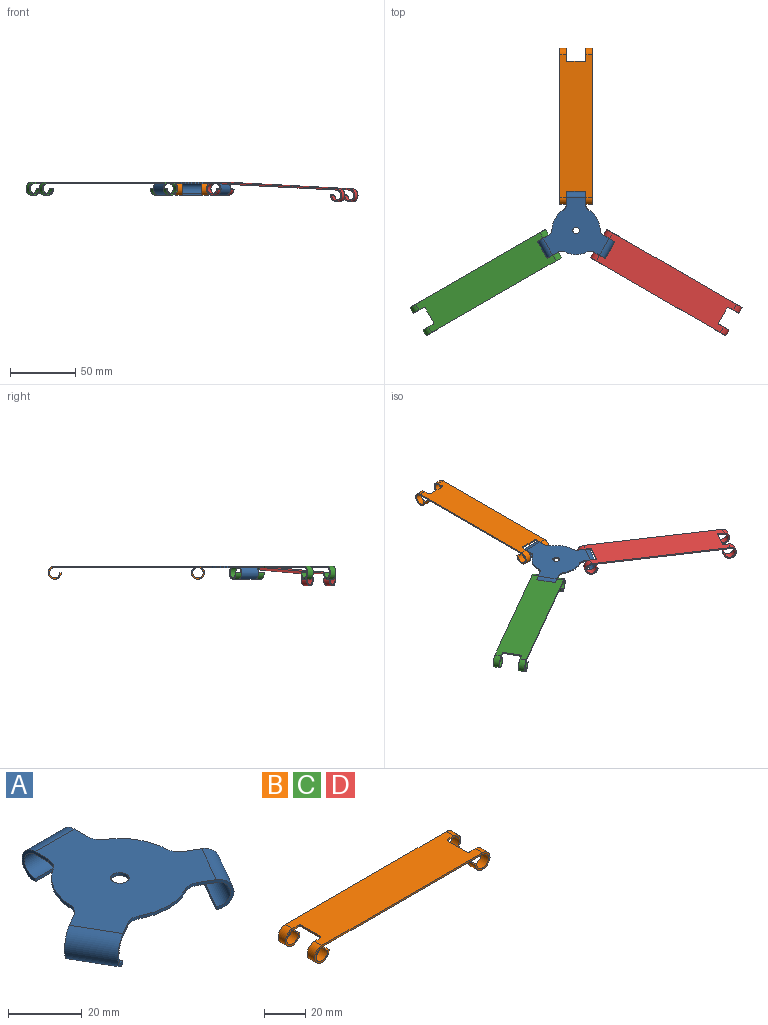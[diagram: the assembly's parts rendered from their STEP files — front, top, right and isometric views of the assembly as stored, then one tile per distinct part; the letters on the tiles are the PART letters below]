
ASSEMBLY  parts=4 mates=3
PART A: 27 faces, bbox 59.5x51.5x10 mm
  f0: cylinder r=18.5mm len=14.98mm, axis (0,0,1), area 18mm2, adj f12,f16,f20,f25
  f1: plane 10x8.75mm, normal (0.5,0.87,0), area 19.2mm2, adj f10,f12,f15,f16,f19,f25
  f2: plane 10x8.75mm, normal (-0.5,-0.87,0), area 19.2mm2, adj f10,f12,f15,f16,f19,f24
  f3: cylinder r=18.5mm len=17.29mm, axis (0,0,1), area 18mm2, adj f12,f16,f23,f24
  f4: plane 10x8.75mm, normal (0.5,-0.87,0), area 19.2mm2, adj f9,f12,f14,f16,f18,f23
  f5: plane 10x8.75mm, normal (-0.5,0.87,0), area 19.2mm2, adj f9,f12,f14,f16,f18,f22
  f6: cylinder r=18.5mm len=14.98mm, axis (0,0,1), area 18mm2, adj f12,f16,f21,f22
  f7: plane 10.1x10mm, normal (-1,0,0), area 19.2mm2, adj f11,f12,f13,f16,f17,f21
  f8: plane 10.1x10mm, normal (1,0,0), area 19.2mm2, adj f11,f12,f13,f16,f17,f20
  f9: plane 12.99x7.5mm, normal (0.87,0.5,0), area 15mm2, adj f4,f5,f14,f18
  f10: plane 12.99x7.5mm, normal (-0.87,0.5,0), area 15mm2, adj f1,f2,f15,f19
  f11: plane 15x1mm, normal (0,-1,0), area 15mm2, adj f7,f8,f13,f17
  f12: plane 50.8x44mm, normal (0,0,1), area 1379.7mm2, adj f0,f1,f2,f3,f4,f5,f6,f7
  f13: cylinder r=5mm len=15mm, axis (1,0,0), area 235.6mm2, adj f7,f8,f11,f12
  f14: cylinder r=5mm len=15.49mm, axis (-0.5,0.87,0), area 235.6mm2, adj f4,f5,f9,f12
  f15: cylinder r=5mm len=15.49mm, axis (-0.5,-0.87,0), area 235.6mm2, adj f1,f2,f10,f12
  f16: plane 50.8x44mm, normal (0,0,-1), area 1379.7mm2, adj f0,f1,f2,f3,f4,f5,f6,f7
  f17: cylinder r=4mm len=15mm, axis (1,0,0), area 188.5mm2, adj f7,f8,f11,f16
  f18: cylinder r=4mm len=14.99mm, axis (-0.5,0.87,0), area 188.5mm2, adj f4,f5,f9,f16
  f19: cylinder r=4mm len=14.99mm, axis (-0.5,-0.87,0), area 188.5mm2, adj f1,f2,f10,f16
  f20: cylinder r=5mm len=4.23mm, axis (0,0,1), area 5mm2, adj f0,f8,f12,f16
  f21: cylinder r=5mm len=4.23mm, axis (0,0,1), area 5mm2, adj f6,f7,f12,f16
  f22: cylinder r=5mm len=4.14mm, axis (0,0,1), area 5mm2, adj f5,f6,f12,f16
  f23: cylinder r=5mm len=4.84mm, axis (0,0,1), area 5mm2, adj f3,f4,f12,f16
  f24: cylinder r=5mm len=4.84mm, axis (0,0,1), area 5mm2, adj f2,f3,f12,f16
  f25: cylinder r=5mm len=4.14mm, axis (0,0,1), area 5mm2, adj f0,f1,f12,f16
  f26: cylinder r=2.5mm len=5mm, axis (0,0,1), area 15.7mm2, adj f12,f16
PART B: 26 faces, bbox 120x25x10 mm
  f0: cylinder r=4mm len=8mm, axis (0,1,0), area 94.2mm2, adj f1,f7,f15,f17
  f1: plane 110x25mm, normal (0,0,-1), area 2600.9mm2, adj f0,f2,f8,f9,f14,f15,f16,f17
  f2: cylinder r=4mm len=8mm, axis (0,1,0), area 94.2mm2, adj f1,f3,f14,f20
  f3: plane 5x1mm, normal (0,0,1), area 5mm2, adj f2,f4,f14,f20
  f4: cylinder r=5mm len=10mm, axis (0,1,0), area 117.8mm2, adj f3,f5,f14,f20
  f5: plane 110x25mm, normal (0,0,1), area 2600.9mm2, adj f4,f6,f11,f12,f14,f15,f16,f17
  f6: cylinder r=5mm len=10mm, axis (0,1,0), area 117.8mm2, adj f5,f7,f15,f17
  f7: plane 5x1mm, normal (0,0,1), area 5mm2, adj f0,f6,f15,f17
  f8: cylinder r=4mm len=8mm, axis (0,1,0), area 94.2mm2, adj f1,f13,f14,f18
  f9: cylinder r=4mm len=8mm, axis (0,1,0), area 94.2mm2, adj f1,f10,f15,f19
  f10: plane 5x1mm, normal (0,0,1), area 5mm2, adj f9,f11,f15,f19
  f11: cylinder r=5mm len=10mm, axis (0,1,0), area 117.8mm2, adj f5,f10,f15,f19
  f12: cylinder r=5mm len=10mm, axis (0,1,0), area 117.8mm2, adj f5,f13,f14,f18
  f13: plane 5x1mm, normal (0,0,1), area 5mm2, adj f8,f12,f14,f18
  f14: plane 120x10mm, normal (0,-1,0), area 152.4mm2, adj f1,f2,f3,f4,f5,f8,f12,f13
  f15: plane 120x10mm, normal (0,1,0), area 152.4mm2, adj f0,f1,f5,f6,f7,f9,f10,f11
  f16: plane 13x1mm, normal (-1,0,0), area 13mm2, adj f1,f5,f24,f25
  f17: plane 10x10mm, normal (0,-1,0), area 25.2mm2, adj f0,f1,f5,f6,f7,f25
  f18: plane 10x10mm, normal (0,1,0), area 25.2mm2, adj f1,f5,f8,f12,f13,f24
  f19: plane 10x10mm, normal (0,-1,0), area 25.2mm2, adj f1,f5,f9,f10,f11,f22
  f20: plane 10x10mm, normal (0,1,0), area 25.2mm2, adj f1,f2,f3,f4,f5,f23
  f21: plane 13x1mm, normal (1,0,0), area 13mm2, adj f1,f5,f22,f23
  f22: cylinder r=1mm len=1mm, axis (0,0,-1), area 1.6mm2, adj f1,f5,f19,f21
  f23: cylinder r=1mm len=1mm, axis (0,0,1), area 1.6mm2, adj f1,f5,f20,f21
  f24: cylinder r=1mm len=1mm, axis (0,0,1), area 1.6mm2, adj f1,f5,f16,f18
  f25: cylinder r=1mm len=1mm, axis (0,0,-1), area 1.6mm2, adj f1,f5,f16,f17
PART C: same geometry as B
PART D: same geometry as B
PLACE A at identity fixed
PLACE B rot(axis=(0,0,-1),90deg) t=(0,30,0)mm
PLACE C rot(axis=(0,0,1),30deg) t=(-69.28,-90,0)mm
PLACE D rot(axis=(0.02,0.09,-1),30.1deg) t=(69.43,-90.09,-2.53)mm
MATE revolute A.f15 <-> D.f0  axis (0.5,0.87,0) through (17.9,-69,-5)mm
MATE revolute B.f2 <-> A.f13  axis (1,0,0) through (-7.5,-25,-5)mm
MATE revolute C.f2 <-> A.f14  axis (-0.5,0.87,0) through (-25.4,-56,-5)mm
